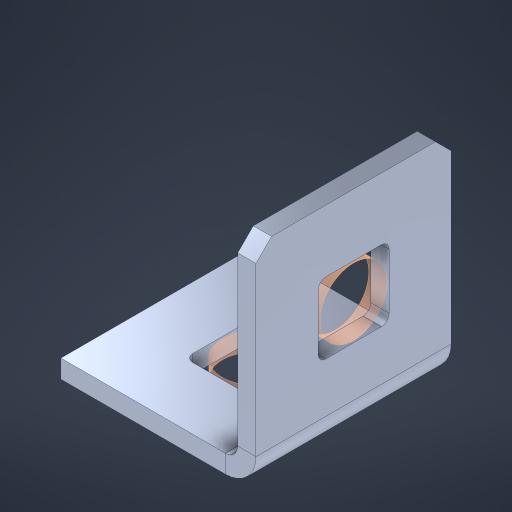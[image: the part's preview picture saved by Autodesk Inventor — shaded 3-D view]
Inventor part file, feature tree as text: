
AUTODESK INVENTOR PART (.ipt)
format: ipt  version: 2023 (Build 270158000, 158)  size: 438,784 bytes
history: native  units: in
note: dims shown in document units (in); Inventor stores cm internally (conversion verified against a paired STEP export)
features: other x75, extrude x69, sheet_metal_op x10, sketch x8, mirror x1, pattern_linear x1, chamfer x1
ambient origin geometry x8: Origin, YZ Plane, XZ Plane, XY Plane, X Axis, Y Axis, Z Axis, Center Point
bodies: Solid1 (feature_tree), Body (feature_tree)
feature tree (165):
  other  "Flange Pattern Plane"
  sheet_metal_op  "Flange Pattern"
  sheet_metal_op  "Body Pattern"
  other  "Arc Length"
  mirror  "Notch Mirror"
  pattern_linear  "Notch Pattern"  Spacing1=0.1875in  [1 undecoded]
  chamfer  "End Chamfer"
  extrude  "Half Cut"  Depth=0.0469in
  sketch  "Sketch1"  dims[d0=2.5in]
  other  "Plate1"
  sketch  "Sketch2"  dims[d1=0.5in]
  other  "Plate2"
  sheet_metal_op  "Bend1"
  sheet_metal_op  "Corner1"
  sketch  "Sketch3"  dims[d2=0.0469in]
  other  "Flange Pattern Sketch"
  sketch  "Sketch7"  dims[d3=0.0469in]
  other  "Srf1"
  other  "Srf2"
  sketch  "Sketch8"  dims[d4=0.0234in]
  sketch  "Sketch9"  dims[d5=0.0938in]
  other  "Srf91"
  sheet_metal_op  "Body Pattern Sketch"
  other  "Srf92"
  sketch  "Sketch13"  dims[d6=0.0469in]
  sketch  "Sketch14"  dims[d7=0.5in d8=90.0deg d9=0.0312in d10=0.1875in d11=0.0469in d12=0.0469in d16=0.182in d17=0.02in d18=0.0469in d19=0.0in d20=0.25in d21=0.25in d46=0.172in d47=1.0in d48=0.0in d49=0.182in d50=0.02in d51=0.25in d52=0.25in d53=0.0469in d54=0.0in d55=0.172in d56=1.0in d57=0.0in d60=0.3937in d62=0.5in d63=0.3937in d65=0.5in d85=0.1227in d86=0.1659in d88=0.04in d89=0.0469in d90=0.0in d91=0.04in d92=0.0491in d95=2.5in d96=0.04in d97=0.25in d98=45.0deg d101=0.0in d102=2.497in d131=0.5in d132=0.3937in d134=0.5in d139=0.5in]
  other  "Srf856"
  other  "Srf1310"
  other  "Srf1311"
  other  "Srf1312"
  other  "Srf1376"
  other  "Srf1377"
  other  "Srf1728"
  other  "Srf1755"
  other  "Srf1878"
  other  "Srf1879"
  other  "Srf1880"
  other  "Srf1881"
  other  "Srf1882"
  other  "Srf1883"
  other  "Srf1884"
  other  "Srf1885"
  other  "Srf1886"
  other  "Srf1887"
  other  "Srf1888"
  other  "Srf1889"
  other  "Srf1890"
  other  "Srf1891"
  other  "Srf1892"
  other  "Srf1893"
  other  "Srf1894"
  other  "Srf1895"
  other  "Srf1896"
  other  "Srf1897"
  other  "Srf1898"
  other  "Srf1899"
  other  "Srf1900"
  other  "Srf1901"
  other  "Srf1902"
  other  "Srf1903"
  other  "Srf1904"
  other  "Srf1905"
  other  "Srf1906"
  other  "Srf1942"
  other  "Srf1943"
  other  "Srf1944"
  other  "Srf1945"
  other  "Srf1946"
  other  "Srf1947"
  other  "Srf1948"
  other  "Srf1949"
  other  "Srf1950"
  other  "Srf1951"
  other  "Srf1952"
  other  "Srf1953"
  other  "Srf1954"
  other  "Srf1955"
  other  "Srf1956"
  other  "Srf1957"
  other  "Srf1958"
  other  "Srf1959"
  other  "Srf1960"
  other  "Srf1961"
  other  "Srf1962"
  other  "Srf1963"
  other  "Srf1964"
  other  "Srf1965"
  other  "Srf1966"
  other  "Srf1967"
  other  "Srf1968"
  other  "Srf1969"
  other  "Srf1970"
  sheet_metal_op  "Flange Stamp"
  sheet_metal_op  "Flange Circle"
  sheet_metal_op  "Body Stamp"
  sheet_metal_op  "Body Circle"
  sheet_metal_op  "Notch"
  extrude  "ExtrusionSrf2"  Depth=0.0469in
  extrude  "ExtrusionSrf92"  Depth=0.182in
  extrude  "ExtrusionSrf856"  Depth=0.02in
  extrude  "ExtrusionSrf1310"  Depth=0.0469in
  extrude  "ExtrusionSrf1311"  TaperAngle=0.0deg  [1 undecoded]
  extrude  "ExtrusionSrf1312"  Depth=0.25in
  extrude  "ExtrusionSrf1376"  Depth=0.25in
  extrude  "ExtrusionSrf1377"  Depth=0.5in
  extrude  "ExtrusionSrf1728"  Depth=0.5in TaperAngle=0.0deg
  extrude  "ExtrusionSrf1755"  Depth=0.182in
  extrude  "ExtrusionSrf1878"  Depth=0.02in
  extrude  "ExtrusionSrf1879"  Depth=0.25in
  extrude  "ExtrusionSrf1880"  Depth=0.25in
  extrude  "ExtrusionSrf1881"  Depth=0.0469in
  extrude  "ExtrusionSrf1882"  TaperAngle=0.0deg  [1 undecoded]
  extrude  "ExtrusionSrf1883"  Depth=0.5in
  extrude  "ExtrusionSrf1884"  Depth=0.5in TaperAngle=0.0deg
  extrude  "ExtrusionSrf1885"  Depth=0.3937in
  extrude  "ExtrusionSrf1886"  Depth=0.5in
  extrude  "ExtrusionSrf1887"  Depth=0.5in
  extrude  "ExtrusionSrf1888"  Depth=0.5in
  extrude  "ExtrusionSrf1889"  Depth=0.5in
  extrude  "ExtrusionSrf1890"  Depth=0.0469in
  extrude  "ExtrusionSrf1891"  TaperAngle=0.0deg  [1 undecoded]
  extrude  "ExtrusionSrf1892"  Depth=0.5in
  extrude  "ExtrusionSrf1893"  Depth=0.5in
  extrude  "ExtrusionSrf1894"  Depth=0.5in
  extrude  "ExtrusionSrf1895"  Depth=0.25in TaperAngle=45.0deg
  extrude  "ExtrusionSrf1896"  TaperAngle=0.0deg  [1 undecoded]
  extrude  "ExtrusionSrf1897"  Depth=0.5in
  extrude  "ExtrusionSrf1898"  Depth=0.5in
  extrude  "ExtrusionSrf1899"  Depth=0.3937in
  extrude  "ExtrusionSrf1900"  Depth=0.5in
  extrude  "ExtrusionSrf1901"  Depth=0.5in
  extrude  "ExtrusionSrf1902"  [1 undecoded]
  extrude  "ExtrusionSrf1903"  [1 undecoded]
  extrude  "ExtrusionSrf1904"  [1 undecoded]
  extrude  "ExtrusionSrf1905"  [1 undecoded]
  extrude  "ExtrusionSrf1906"  [1 undecoded]
  extrude  "ExtrusionSrf1942"  [1 undecoded]
  extrude  "ExtrusionSrf1943"  [1 undecoded]
  extrude  "ExtrusionSrf1944"  [1 undecoded]
  extrude  "ExtrusionSrf1945"  [1 undecoded]
  extrude  "ExtrusionSrf1946"  [1 undecoded]
  extrude  "ExtrusionSrf1947"  [1 undecoded]
  extrude  "ExtrusionSrf1948"  [1 undecoded]
  extrude  "ExtrusionSrf1949"  [1 undecoded]
  extrude  "ExtrusionSrf1950"  [1 undecoded]
  extrude  "ExtrusionSrf1951"  [1 undecoded]
  extrude  "ExtrusionSrf1952"  [1 undecoded]
  extrude  "ExtrusionSrf1953"  [1 undecoded]
  extrude  "ExtrusionSrf1954"  [1 undecoded]
  extrude  "ExtrusionSrf1955"  [1 undecoded]
  extrude  "ExtrusionSrf1956"  [1 undecoded]
  extrude  "ExtrusionSrf1957"  [1 undecoded]
  extrude  "ExtrusionSrf1958"  [1 undecoded]
  extrude  "ExtrusionSrf1959"  [1 undecoded]
  extrude  "ExtrusionSrf1960"  [1 undecoded]
  extrude  "ExtrusionSrf1961"  [1 undecoded]
  extrude  "ExtrusionSrf1962"  [1 undecoded]
  extrude  "ExtrusionSrf1963"  [1 undecoded]
  extrude  "ExtrusionSrf1964"  [1 undecoded]
  extrude  "ExtrusionSrf1965"  [1 undecoded]
  extrude  "ExtrusionSrf1966"  [1 undecoded]
  extrude  "ExtrusionSrf1967"  [1 undecoded]
  extrude  "ExtrusionSrf1968"  [1 undecoded]
  extrude  "ExtrusionSrf1969"  [1 undecoded]
  extrude  "ExtrusionSrf1970"  [1 undecoded]
note: 39 required parameter values undecoded (feature->parameter linkage not recoverable at this tier; creation-order binding heuristic only, values carry confidence <= 0.55)
